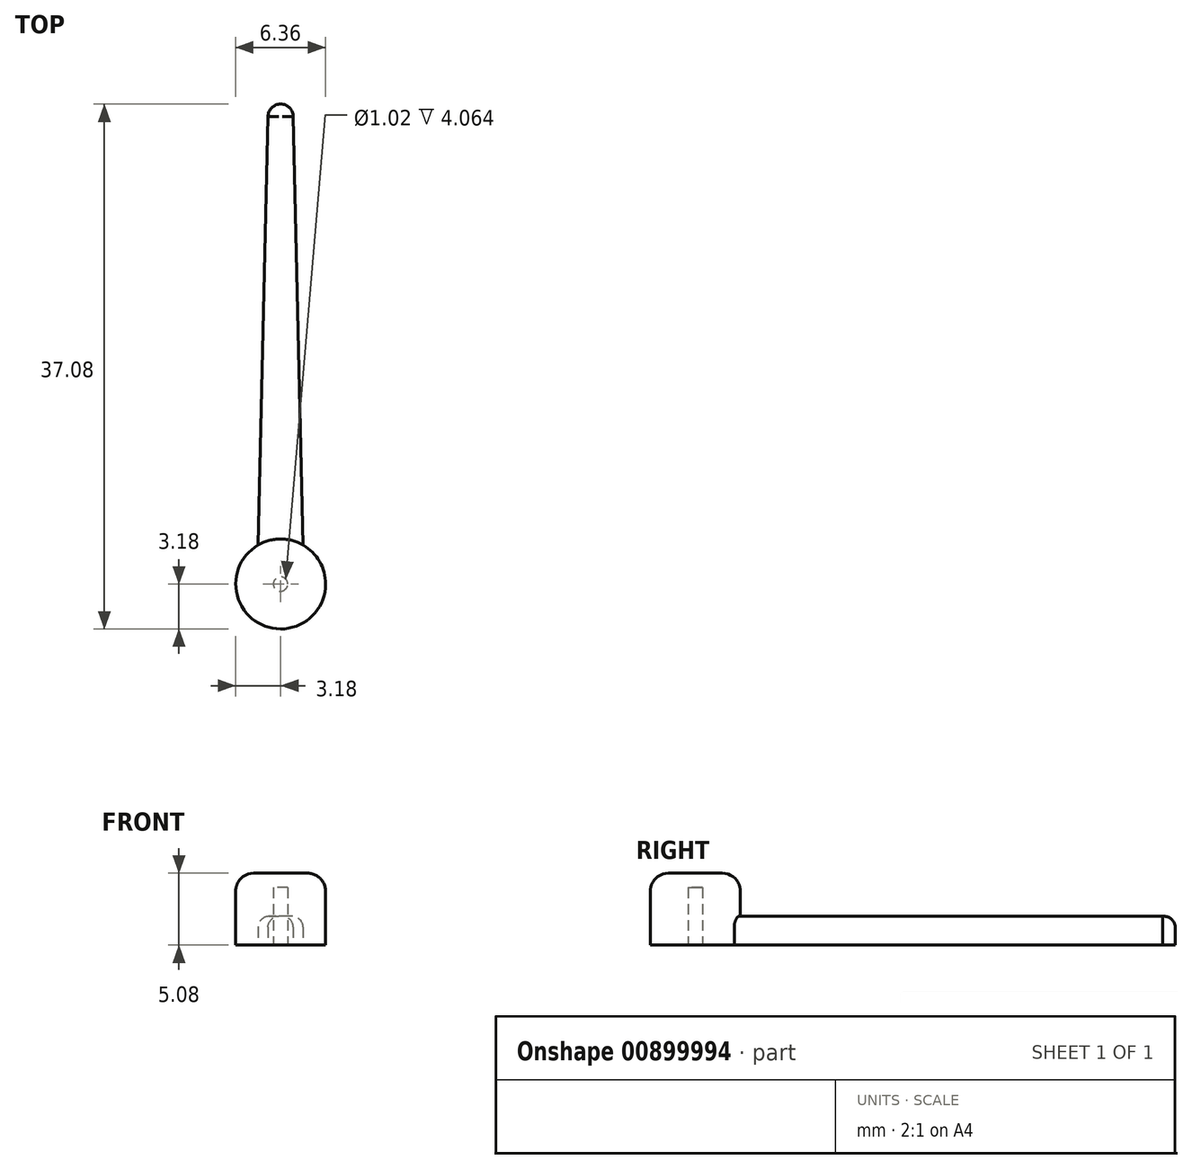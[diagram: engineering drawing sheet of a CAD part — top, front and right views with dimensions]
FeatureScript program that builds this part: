
annotation { "Feature Type Name" : "Feature", "Feature Type Description" : "" }
export const myFeature = defineFeature(function(context is Context, id is Id, definition is map)
    precondition{}
    {
        {
            var Q0;
            Q0=qCreatedBy(makeId("Top.planeOp"),FACE);
            var sketch = newSketch(context, id + "F0", { "sketchPlane" : qUnion([Q0])});
            skLineSegment(sketch, "E0", {"start": v(0, 0) * mm, "end": v(-1.65, 0) * mm});
            skLineSegment(sketch, "E1", {"start": v(0, 0) * mm, "end": v(1.65, 0) * mm});
            skCircle(sketch, "E2", {"center": v(0, 0) * mm, "radius": 3.18 * mm});
            skLineSegment(sketch, "E3", {"start": v(-1.65, 0) * mm, "end": v(-0.89, 33.01) * mm});
            skLineSegment(sketch, "E4", {"start": v(1.65, 0) * mm, "end": v(0.89, 33.01) * mm});
            skLineSegment(sketch, "E5", {"start": v(0.89, 33.01) * mm, "end": v(-0.89, 33.01) * mm});
            skCircle(sketch, "E6", {"center": v(0, 33.01) * mm, "radius": 0.89 * mm});
            skSolve(sketch);
        }
        {
            var Q0;
            {var subQ1=sQuery(id+"F0.wireOp",EDGE,"E0");Q0=makeQuery(id+"F0.imprint","IMPRINT",FACE,{"disambiguationData":[TD([[makeQuery(id+"F0.imprint","IMPRINT",EDGE,{"derivedFrom":subQ1}),1.0]])]});}
            var Q1;
            {var subQ1=sQuery(id+"F0.wireOp",EDGE,"E0");Q1=makeQuery(id+"F0.imprint","IMPRINT",FACE,{"disambiguationData":[TD([[makeQuery(id+"F0.imprint","IMPRINT",EDGE,{"derivedFrom":subQ1}),-1.0]])]});}
            extrude(context, id + "F1", {"entities" : qUnion([Q0, Q1]), "depth" : 5.08 * mm, "offsetDistance" : 25.4 * mm});
        }
        {
            var Q0;
            Q0=makeQuery(id+"F1.opExtrude","CAP_EDGE",EDGE,{"disambiguationData":[OSD([sQuery(id+"F0.wireOp",EDGE,"E2")])],"isStart":false});
            fillet(context, id + "F2", {"entities" : qUnion([Q0]), "radius" : 1.27 * mm, "tangentPropagation" : true, "allowEdgeOverflow" : false});
        }
        {
            var Q0;
            Q0=qCreatedBy(makeId("Top.planeOp"),FACE);
            var sketch = newSketch(context, id + "F3", { "sketchPlane" : qUnion([Q0])});
            skCircle(sketch, "E7", {"center": v(0, 0) * mm, "radius": 0.5 * mm});
            skSolve(sketch);
        }
        {
            var Q0;
            Q0=qSketchRegion(id+"F3",true);
            extrude(context, id + "F4", {"entities" : qUnion([Q0]), "operationType" : NewBodyOperationType.REMOVE, "depth" : 4.06 * mm, "offsetDistance" : 25.4 * mm});
        }
        {
            var Q0;
            {var subQ0=sQuery(id+"F0.wireOp",EDGE,"E3");var subQ1=sQuery(id+"F0.wireOp",EDGE,"E2");var subQ2=makeQuery(id+"F0.imprint","INTERSECT",VERTEX,{"derivedFrom":[subQ1,subQ0]});Q0=makeQuery(id+"F0.imprint","IMPRINT",FACE,{"disambiguationData":[TD([[makeQuery(id+"F0.imprint","IMPRINT",EDGE,{"disambiguationData":[TD([[subQ2,1.0]])],"derivedFrom":subQ1}),-1.0]])]});}
            var Q1;
            {var subQ0=sQuery(id+"F0.wireOp",EDGE,"E5");Q1=makeQuery(id+"F0.imprint","IMPRINT",FACE,{"disambiguationData":[TD([[makeQuery(id+"F0.imprint","IMPRINT",EDGE,{"derivedFrom":subQ0}),-1.0]])]});}
            var Q2;
            {var subQ0=sQuery(id+"F0.wireOp",EDGE,"E5");Q2=makeQuery(id+"F0.imprint","IMPRINT",FACE,{"disambiguationData":[TD([[makeQuery(id+"F0.imprint","IMPRINT",EDGE,{"derivedFrom":subQ0}),1.0]])]});}
            extrude(context, id + "F5", {"entities" : qUnion([Q0, Q1, Q2]), "operationType" : NewBodyOperationType.ADD, "depth" : 2.03 * mm, "offsetDistance" : 25.4 * mm});
        }
        {
            var Q0;
            Q0=makeQuery(id+"F5.opExtrude","CAP_EDGE",EDGE,{"disambiguationData":[OSD([sQuery(id+"F0.wireOp",EDGE,"E3")])],"isStart":false});
            var Q1;
            Q1=makeQuery(id+"F5.opExtrude","CAP_EDGE",EDGE,{"disambiguationData":[OSD([sQuery(id+"F0.wireOp",EDGE,"E4")])],"isStart":false});
            var Q2;
            Q2=makeQuery(id+"F5.opExtrude","CAP_EDGE",EDGE,{"disambiguationData":[OSD([sQuery(id+"F0.wireOp",EDGE,"E6")])],"isStart":false});
            fillet(context, id + "F6", {"entities" : qUnion([Q0, Q1, Q2]), "radius" : 0.76 * mm, "tangentPropagation" : true, "allowEdgeOverflow" : false});
        }
    });
